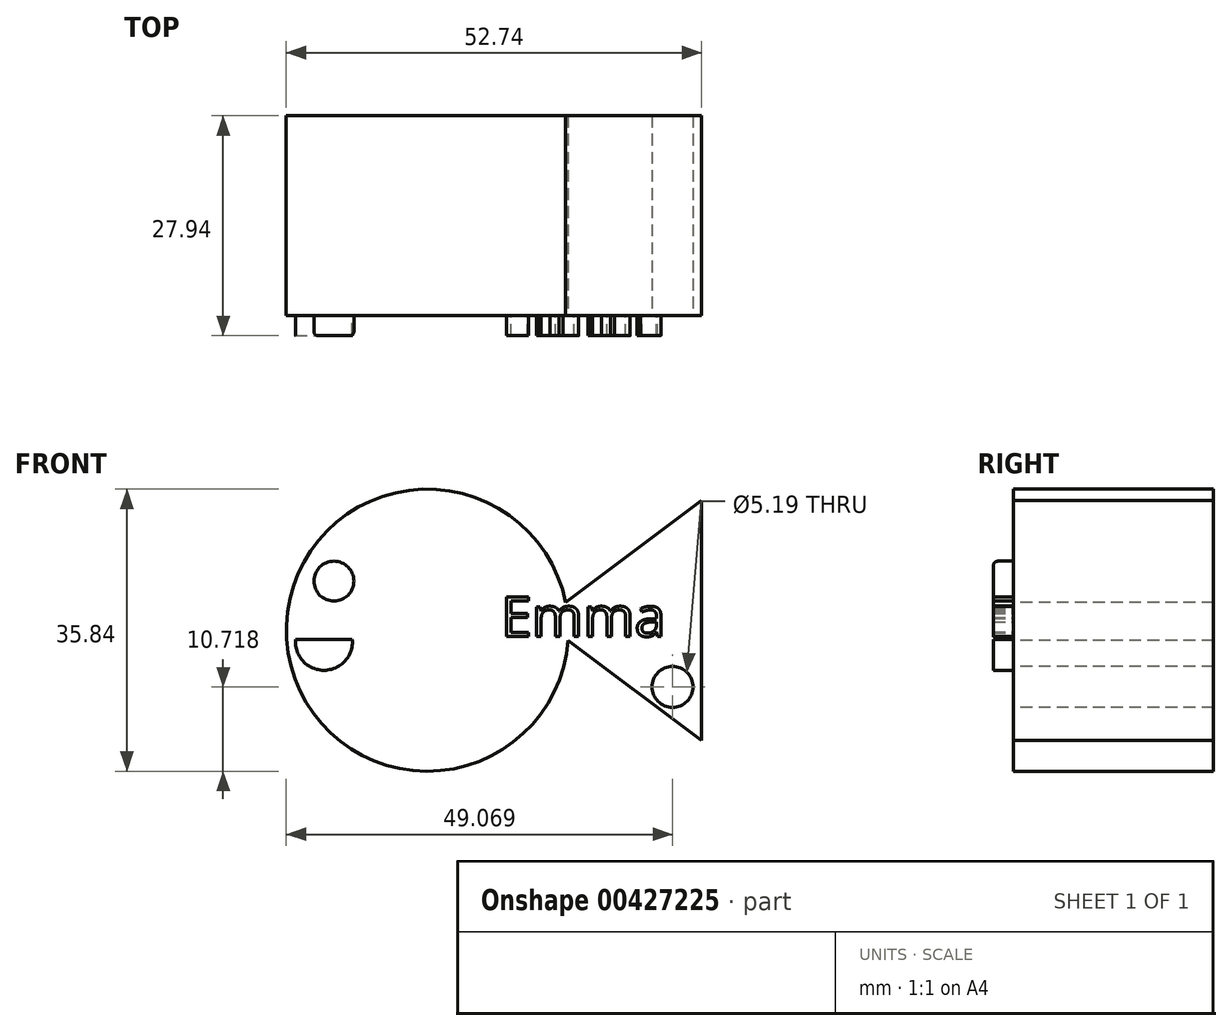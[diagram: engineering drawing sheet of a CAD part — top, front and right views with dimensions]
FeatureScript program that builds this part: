
annotation { "Feature Type Name" : "Feature", "Feature Type Description" : "" }
export const myFeature = defineFeature(function(context is Context, id is Id, definition is map)
    precondition{}
    {
        {
            var Q0;
            Q0=qCreatedBy(makeId("Front.planeOp"),FACE);
            var sketch = newSketch(context, id + "F0", { "sketchPlane" : qUnion([Q0])});
            skCircle(sketch, "E0", {"center": v(14.2, 20.05) * mm, "radius": 17.92 * mm});
            skLineSegment(sketch, "E1", {"start": v(28.71, 21.28) * mm, "end": v(49.03, 36.52) * mm});
            skLineSegment(sketch, "E2", {"start": v(49.03, 36.52) * mm, "end": v(49.03, 6.04) * mm});
            skLineSegment(sketch, "E3", {"start": v(49.03, 6.04) * mm, "end": v(28.71, 21.28) * mm});
            skSolve(sketch);
        }
        {
            var Q0;
            Q0 = qSketchRegion(id + "F0", true);
            extrude(context, id + "F1", {"entities" : qUnion([Q0]), "oppositeDirection" : true, "depth" : 25.4 * mm});
        }
        {
            var Q0;
            Q0=qCreatedBy(makeId("Front.planeOp"),FACE);
            var sketch = newSketch(context, id + "F2", { "sketchPlane" : qUnion([Q0])});
            skCircle(sketch, "E4", {"center": v(2.34, 26.28) * mm, "radius": 2.53 * mm});
            skSolve(sketch);
        }
        {
            var Q0;
            Q0 = qSketchRegion(id + "F2", true);
            extrude(context, id + "F3", {"entities" : qUnion([Q0]), "operationType" : NewBodyOperationType.ADD, "depth" : 2.54 * mm});
        }
        {
            var Q0;
            Q0=qCreatedBy(makeId("Front.planeOp"),FACE);
            var sketch = newSketch(context, id + "F4", { "sketchPlane" : qUnion([Q0])});
            skLineSegment(sketch, "E5", {"start": v(-2.53, 18.88) * mm, "end": v(4.67, 18.88) * mm});
            skArc(sketch, "E6", {"start": v(-2.53, 18.88) * mm, "mid": v(1.07, 14.96) * mm, "end": v(4.67, 18.88) * mm});
            skSolve(sketch);
        }
        {
            var Q0;
            Q0=makeQuery(id+"F4.imprint","IMPRINT",FACE,{"disambiguationData":[TD([[makeQuery(id+"F4.imprint","IMPRINT",EDGE,{"derivedFrom":sQuery(id+"F4.wireOp",EDGE,"E5")}),-1.0]])]});
            extrude(context, id + "F5", {"entities" : qUnion([Q0]), "operationType" : NewBodyOperationType.ADD, "depth" : 2.54 * mm});
        }
        {
            var Q0;
            Q0=qCreatedBy(makeId("Front.planeOp"),FACE);
            var sketch = newSketch(context, id + "F6", { "sketchPlane" : qUnion([Q0])});
            skText(sketch, "E7", { "text": "Emma", "fontName": "OpenSans-Regular.ttf"});
            const initialGuessF6  = {"E7": [0.02356, 0.01927, 1, 0, 0.00506]};
            skSetInitialGuess(sketch, initialGuessF6);
            skSolve(sketch);
        }
        {
            var Q0;
            Q0 = qSketchRegion(id + "F6", true);
            extrude(context, id + "F7", {"entities" : qUnion([Q0]), "operationType" : NewBodyOperationType.ADD, "depth" : 2.54 * mm});
        }
        {
            var Q0;
            Q0=qCreatedBy(makeId("Front.planeOp"),FACE);
            var sketch = newSketch(context, id + "F8", { "sketchPlane" : qUnion([Q0])});
            skCircle(sketch, "E8", {"center": v(45.36, 12.85) * mm, "radius": 2.6 * mm});
            skSolve(sketch);
        }
        {
            var Q0;
            Q0 = qSketchRegion(id + "F8", true);
            extrude(context, id + "F9", {"entities" : qUnion([Q0]), "operationType" : NewBodyOperationType.REMOVE, "oppositeDirection" : true, "depth" : 25.4 * mm});
        }
        {
            var Q0;
            Q0=makeQuery(id+"F3.opExtrude","CAP_EDGE",EDGE,{"disambiguationData":[OSD([sQuery(id+"F2.wireOp",EDGE,"E4")])],"isStart":false});
            fillet(context, id + "F10", {"entities" : qUnion([Q0]), "radius" : 0.5 * mm, "tangentPropagation" : true, "allowEdgeOverflow" : false});
        }
    });
